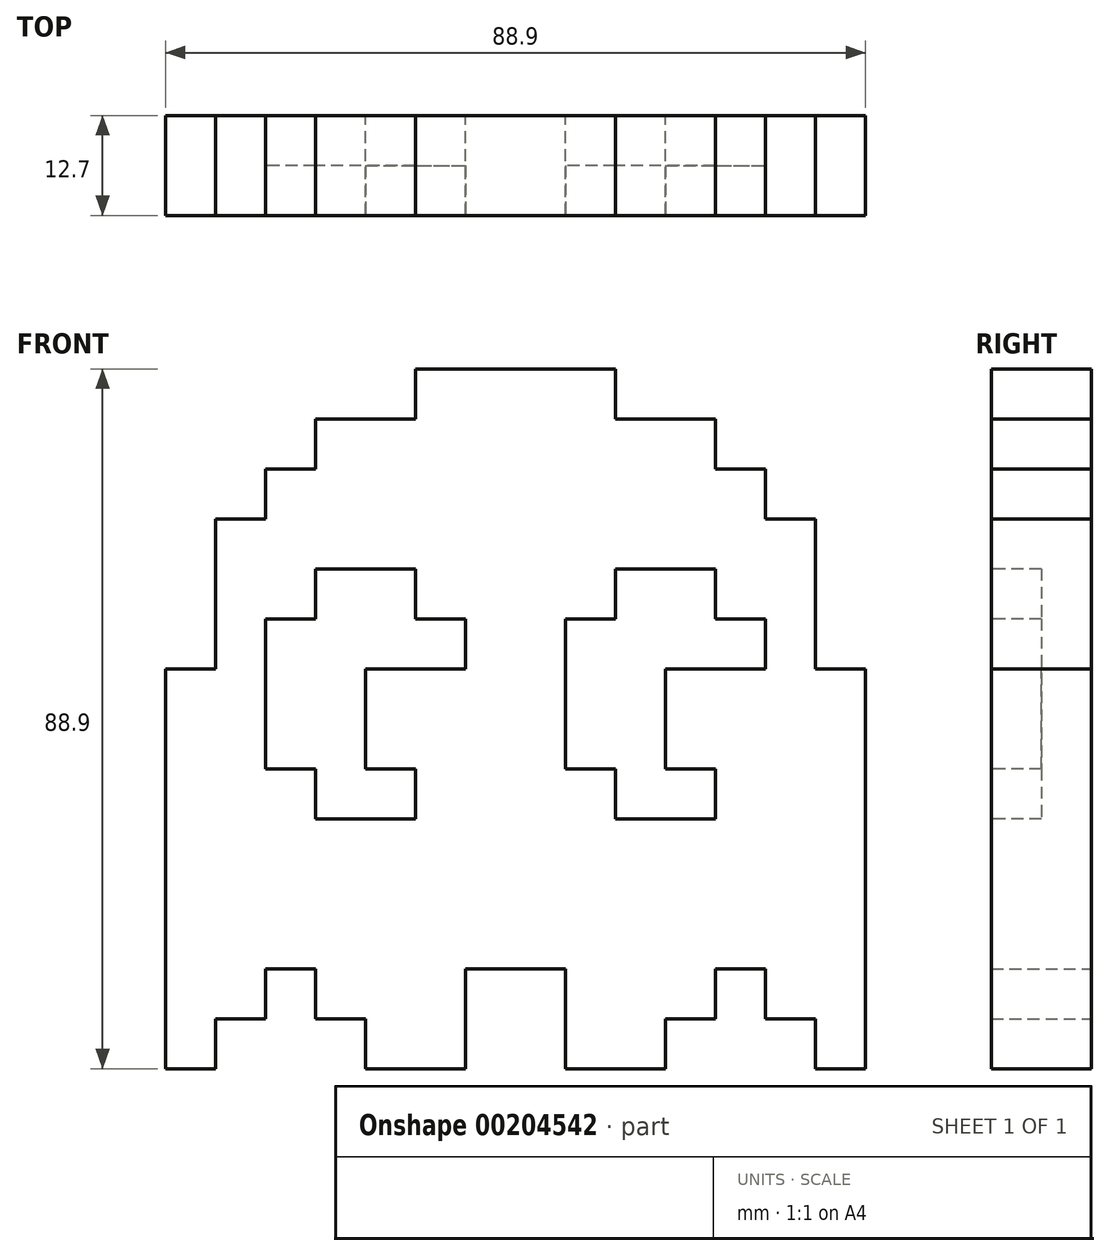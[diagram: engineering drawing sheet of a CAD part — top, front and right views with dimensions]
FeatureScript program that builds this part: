
annotation { "Feature Type Name" : "Feature", "Feature Type Description" : "" }
export const myFeature = defineFeature(function(context is Context, id is Id, definition is map)
    precondition{}
    {
        {
            var Q0;
            Q0=qCreatedBy(makeId("Front.planeOp"),FACE);
            var sketch = newSketch(context, id + "F0", { "sketchPlane" : qUnion([Q0])});
            skLineSegment(sketch, "E0", {"start": v(-26.41, 0) * mm, "end": v(-1.01, 0) * mm});
            skLineSegment(sketch, "E1", {"start": v(-26.41, 0) * mm, "end": v(-26.41, -6.35) * mm});
            skLineSegment(sketch, "E2", {"start": v(-1.01, 0) * mm, "end": v(-1.01, -6.35) * mm});
            skLineSegment(sketch, "E3", {"start": v(-26.41, -6.35) * mm, "end": v(-39.11, -6.35) * mm});
            skLineSegment(sketch, "E4", {"start": v(-1.01, -6.35) * mm, "end": v(11.69, -6.35) * mm});
            skLineSegment(sketch, "E5", {"start": v(-39.11, -6.35) * mm, "end": v(-39.11, -12.7) * mm});
            skLineSegment(sketch, "E6", {"start": v(11.69, -6.35) * mm, "end": v(11.69, -12.7) * mm});
            skLineSegment(sketch, "E7", {"start": v(-39.11, -12.7) * mm, "end": v(-45.46, -12.7) * mm});
            skLineSegment(sketch, "E8", {"start": v(11.69, -12.7) * mm, "end": v(18.04, -12.7) * mm});
            skLineSegment(sketch, "E9", {"start": v(-45.46, -12.7) * mm, "end": v(-45.46, -19.05) * mm});
            skLineSegment(sketch, "E10", {"start": v(18.04, -12.7) * mm, "end": v(18.04, -19.05) * mm});
            skLineSegment(sketch, "E11", {"start": v(-45.46, -19.05) * mm, "end": v(-51.81, -19.05) * mm});
            skLineSegment(sketch, "E12", {"start": v(18.04, -19.05) * mm, "end": v(24.39, -19.05) * mm});
            skLineSegment(sketch, "E13", {"start": v(-51.81, -19.05) * mm, "end": v(-51.81, -38.1) * mm});
            skLineSegment(sketch, "E14", {"start": v(24.39, -19.05) * mm, "end": v(24.39, -38.1) * mm});
            skLineSegment(sketch, "E15", {"start": v(-51.81, -38.1) * mm, "end": v(-58.16, -38.1) * mm});
            skLineSegment(sketch, "E16", {"start": v(24.39, -38.1) * mm, "end": v(30.74, -38.1) * mm});
            skLineSegment(sketch, "E17", {"start": v(-58.16, -38.1) * mm, "end": v(-58.16, -88.9) * mm});
            skLineSegment(sketch, "E18", {"start": v(30.74, -38.1) * mm, "end": v(30.74, -88.9) * mm});
            skLineSegment(sketch, "E19", {"start": v(-58.16, -88.9) * mm, "end": v(-51.81, -88.9) * mm});
            skLineSegment(sketch, "E20", {"start": v(30.74, -88.9) * mm, "end": v(24.39, -88.9) * mm});
            skLineSegment(sketch, "E21", {"start": v(-51.81, -88.9) * mm, "end": v(-51.81, -82.55) * mm});
            skLineSegment(sketch, "E22", {"start": v(24.39, -88.9) * mm, "end": v(24.39, -82.55) * mm});
            skLineSegment(sketch, "E23", {"start": v(-51.81, -82.55) * mm, "end": v(-45.46, -82.55) * mm});
            skLineSegment(sketch, "E24", {"start": v(24.39, -82.55) * mm, "end": v(18.04, -82.55) * mm});
            skLineSegment(sketch, "E25", {"start": v(-45.46, -82.55) * mm, "end": v(-45.46, -76.2) * mm});
            skLineSegment(sketch, "E26", {"start": v(18.04, -82.55) * mm, "end": v(18.04, -76.2) * mm});
            skLineSegment(sketch, "E27", {"start": v(-45.46, -76.2) * mm, "end": v(-39.11, -76.2) * mm});
            skLineSegment(sketch, "E28", {"start": v(18.04, -76.2) * mm, "end": v(11.69, -76.2) * mm});
            skLineSegment(sketch, "E29", {"start": v(-39.11, -76.2) * mm, "end": v(-39.11, -82.55) * mm});
            skLineSegment(sketch, "E30", {"start": v(11.69, -76.2) * mm, "end": v(11.69, -82.55) * mm});
            skLineSegment(sketch, "E31", {"start": v(11.69, -82.55) * mm, "end": v(5.34, -82.55) * mm});
            skLineSegment(sketch, "E32", {"start": v(-39.11, -82.55) * mm, "end": v(-32.76, -82.55) * mm});
            skLineSegment(sketch, "E33", {"start": v(-32.76, -82.55) * mm, "end": v(-32.76, -88.9) * mm});
            skLineSegment(sketch, "E34", {"start": v(5.34, -82.55) * mm, "end": v(5.34, -88.9) * mm});
            skLineSegment(sketch, "E35", {"start": v(-32.76, -88.9) * mm, "end": v(-20.06, -88.9) * mm});
            skLineSegment(sketch, "E36", {"start": v(5.34, -88.9) * mm, "end": v(-7.36, -88.9) * mm});
            skLineSegment(sketch, "E37", {"start": v(-20.06, -88.9) * mm, "end": v(-20.06, -76.2) * mm});
            skLineSegment(sketch, "E38", {"start": v(-7.36, -88.9) * mm, "end": v(-7.36, -76.2) * mm});
            skLineSegment(sketch, "E39", {"start": v(-20.06, -76.2) * mm, "end": v(-7.36, -76.2) * mm});
            skSolve(sketch);
        }
        {
            var Q0;
            Q0=makeQuery(id+"F0.imprint","IMPRINT",FACE,{"disambiguationData":[TD([[makeQuery(id+"F0.imprint","IMPRINT",EDGE,{"derivedFrom":sQuery(id+"F0.wireOp",EDGE,"E0")}),-1.0]])]});
            extrude(context, id + "F1", {"entities" : qUnion([Q0]), "depth" : 12.7 * mm});
        }
        {
            var Q0;
            Q0=makeQuery(id+"F1.opExtrude","CAP_FACE",FACE,{"disambiguationData":[OSD([sQuery(id+"F0.wireOp",EDGE,"E0"),sQuery(id+"F0.wireOp",EDGE,"E1"),sQuery(id+"F0.wireOp",EDGE,"E2"),sQuery(id+"F0.wireOp",EDGE,"E3"),sQuery(id+"F0.wireOp",EDGE,"E4"),sQuery(id+"F0.wireOp",EDGE,"E5"),sQuery(id+"F0.wireOp",EDGE,"E6"),sQuery(id+"F0.wireOp",EDGE,"E7"),sQuery(id+"F0.wireOp",EDGE,"E8"),sQuery(id+"F0.wireOp",EDGE,"E9"),sQuery(id+"F0.wireOp",EDGE,"E10"),sQuery(id+"F0.wireOp",EDGE,"E11"),sQuery(id+"F0.wireOp",EDGE,"E12"),sQuery(id+"F0.wireOp",EDGE,"E13"),sQuery(id+"F0.wireOp",EDGE,"E14"),sQuery(id+"F0.wireOp",EDGE,"E15"),sQuery(id+"F0.wireOp",EDGE,"E16"),sQuery(id+"F0.wireOp",EDGE,"E17"),sQuery(id+"F0.wireOp",EDGE,"E18"),sQuery(id+"F0.wireOp",EDGE,"E19"),sQuery(id+"F0.wireOp",EDGE,"E20"),sQuery(id+"F0.wireOp",EDGE,"E21"),sQuery(id+"F0.wireOp",EDGE,"E22"),sQuery(id+"F0.wireOp",EDGE,"E23"),sQuery(id+"F0.wireOp",EDGE,"E24"),sQuery(id+"F0.wireOp",EDGE,"E25"),sQuery(id+"F0.wireOp",EDGE,"E26"),sQuery(id+"F0.wireOp",EDGE,"E27"),sQuery(id+"F0.wireOp",EDGE,"E28"),sQuery(id+"F0.wireOp",EDGE,"E29"),sQuery(id+"F0.wireOp",EDGE,"E30"),sQuery(id+"F0.wireOp",EDGE,"E31"),sQuery(id+"F0.wireOp",EDGE,"E32"),sQuery(id+"F0.wireOp",EDGE,"E33"),sQuery(id+"F0.wireOp",EDGE,"E34"),sQuery(id+"F0.wireOp",EDGE,"E35"),sQuery(id+"F0.wireOp",EDGE,"E36"),sQuery(id+"F0.wireOp",EDGE,"E37"),sQuery(id+"F0.wireOp",EDGE,"E38"),sQuery(id+"F0.wireOp",EDGE,"E39")])],"isStart":false});
            var sketch = newSketch(context, id + "F2", { "sketchPlane" : qUnion([Q0])});
            skLineSegment(sketch, "E40", {"start": v(11.69, -25.4) * mm, "end": v(-1.01, -25.4) * mm});
            skLineSegment(sketch, "E41", {"start": v(-1.01, -25.4) * mm, "end": v(-1.01, -31.75) * mm});
            skLineSegment(sketch, "E42", {"start": v(-1.01, -31.75) * mm, "end": v(-7.36, -31.75) * mm});
            skLineSegment(sketch, "E43", {"start": v(-7.36, -31.75) * mm, "end": v(-7.36, -50.8) * mm});
            skLineSegment(sketch, "E44", {"start": v(11.69, -25.4) * mm, "end": v(11.69, -31.75) * mm});
            skLineSegment(sketch, "E45", {"start": v(11.69, -31.75) * mm, "end": v(18.04, -31.75) * mm});
            skLineSegment(sketch, "E46", {"start": v(18.04, -31.75) * mm, "end": v(18.04, -38.1) * mm});
            skLineSegment(sketch, "E47", {"start": v(-7.36, -50.8) * mm, "end": v(-1.01, -50.8) * mm});
            skLineSegment(sketch, "E48", {"start": v(-1.01, -50.8) * mm, "end": v(-1.01, -57.15) * mm});
            skLineSegment(sketch, "E49", {"start": v(11.69, -50.8) * mm, "end": v(11.69, -57.15) * mm});
            skLineSegment(sketch, "E50", {"start": v(-1.01, -57.15) * mm, "end": v(11.69, -57.15) * mm});
            skLineSegment(sketch, "E51", {"start": v(-26.41, -31.75) * mm, "end": v(-26.41, -25.4) * mm});
            skLineSegment(sketch, "E52", {"start": v(-26.41, -25.4) * mm, "end": v(-39.11, -25.4) * mm});
            skLineSegment(sketch, "E53", {"start": v(-39.11, -25.4) * mm, "end": v(-39.11, -31.75) * mm});
            skLineSegment(sketch, "E54", {"start": v(-26.41, -31.75) * mm, "end": v(-20.06, -31.75) * mm});
            skLineSegment(sketch, "E55", {"start": v(-39.11, -31.75) * mm, "end": v(-45.46, -31.75) * mm});
            skLineSegment(sketch, "E56", {"start": v(-45.46, -31.75) * mm, "end": v(-45.46, -50.8) * mm});
            skLineSegment(sketch, "E57", {"start": v(-20.06, -31.75) * mm, "end": v(-20.06, -38.1) * mm});
            skLineSegment(sketch, "E58", {"start": v(-45.46, -50.8) * mm, "end": v(-39.11, -50.8) * mm});
            skLineSegment(sketch, "E59", {"start": v(-39.11, -50.8) * mm, "end": v(-39.11, -57.15) * mm});
            skLineSegment(sketch, "E60", {"start": v(-26.41, -50.8) * mm, "end": v(-26.41, -57.15) * mm});
            skLineSegment(sketch, "E61", {"start": v(-39.11, -57.15) * mm, "end": v(-26.41, -57.15) * mm});
            skLineSegment(sketch, "E62", {"start": v(-26.41, -50.8) * mm, "end": v(-32.76, -50.8) * mm});
            skPoint(sketch, "E62.endSnap0", {"position": v(-32.76, -6.35) * mm});
            skLineSegment(sketch, "E63", {"start": v(-32.76, -50.8) * mm, "end": v(-32.76, -38.1) * mm});
            skLineSegment(sketch, "E64", {"start": v(-32.76, -38.1) * mm, "end": v(-20.06, -38.1) * mm});
            skPoint(sketch, "E65.start.orphan", {"position": v(-20.06, -50.8) * mm});
            skLineSegment(sketch, "E66", {"start": v(11.69, -50.8) * mm, "end": v(5.34, -50.8) * mm});
            skLineSegment(sketch, "E67", {"start": v(5.34, -50.8) * mm, "end": v(5.34, -38.1) * mm});
            skLineSegment(sketch, "E68", {"start": v(5.34, -38.1) * mm, "end": v(18.04, -38.1) * mm});
            skSolve(sketch);
        }
        {
            var Q0;
            Q0=makeQuery(id+"F2.imprint","IMPRINT",FACE,{"disambiguationData":[TD([[makeQuery(id+"F2.imprint","IMPRINT",EDGE,{"derivedFrom":sQuery(id+"F2.wireOp",EDGE,"E51")}),1.0]])]});
            var Q1;
            Q1=makeQuery(id+"F2.imprint","IMPRINT",FACE,{"disambiguationData":[TD([[makeQuery(id+"F2.imprint","IMPRINT",EDGE,{"derivedFrom":sQuery(id+"F2.wireOp",EDGE,"E40")}),1.0]])]});
            extrude(context, id + "F3", {"entities" : qUnion([Q0, Q1]), "operationType" : NewBodyOperationType.REMOVE, "oppositeDirection" : true, "depth" : 6.35 * mm});
        }
    });
